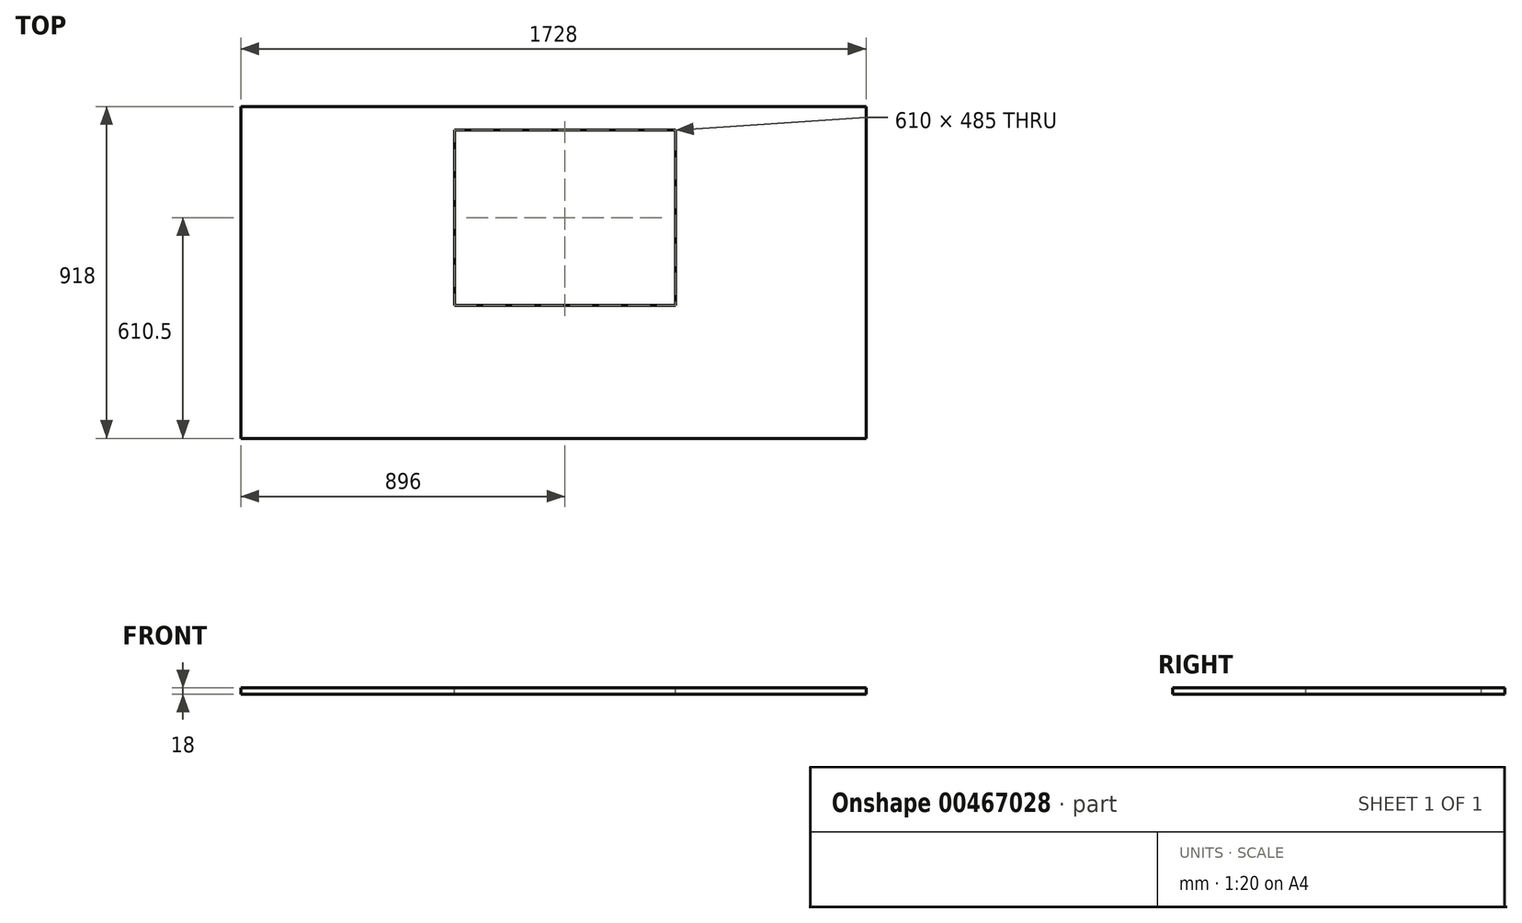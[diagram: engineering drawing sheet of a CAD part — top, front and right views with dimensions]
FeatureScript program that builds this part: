
annotation { "Feature Type Name" : "Feature", "Feature Type Description" : "" }
export const myFeature = defineFeature(function(context is Context, id is Id, definition is map)
    precondition{}
    {
        {
            var Q0;
            Q0=qCreatedBy(makeId("Top.planeOp"),FACE);
            var sketch = newSketch(context, id + "F0", { "sketchPlane" : qUnion([Q0])});
            skLineSegment(sketch, "E0.bottom", {"start": v(0, 918) * mm, "end": v(1728, 918) * mm});
            skLineSegment(sketch, "E0.top", {"start": v(0, 0) * mm, "end": v(1728, 0) * mm});
            skLineSegment(sketch, "E0.left", {"start": v(0, 918) * mm, "end": v(0, 0) * mm});
            skLineSegment(sketch, "E0.right", {"start": v(1728, 918) * mm, "end": v(1728, 0) * mm});
            skSolve(sketch);
        }
        {
            var Q0;
            Q0 = qSketchRegion(id + "F0", true);
            extrude(context, id + "F1", {"entities" : qUnion([Q0]), "depth" : 18 * mm});
        }
        {
            var Q0;
            Q0=makeQuery(id+"F1.opExtrude","CAP_FACE",FACE,{"disambiguationData":[OSD([sQuery(id+"F0.wireOp",EDGE,"E0.bottom"),sQuery(id+"F0.wireOp",EDGE,"E0.top"),sQuery(id+"F0.wireOp",EDGE,"E0.left"),sQuery(id+"F0.wireOp",EDGE,"E0.right")])],"isStart":false});
            var sketch = newSketch(context, id + "F2", { "sketchPlane" : qUnion([Q0])});
            skLineSegment(sketch, "E1.bottom", {"start": v(591, 853) * mm, "end": v(1201, 853) * mm});
            skLineSegment(sketch, "E1.top", {"start": v(591, 368) * mm, "end": v(1201, 368) * mm});
            skLineSegment(sketch, "E1.left", {"start": v(591, 853) * mm, "end": v(591, 368) * mm});
            skLineSegment(sketch, "E1.right", {"start": v(1201, 853) * mm, "end": v(1201, 368) * mm});
            skSolve(sketch);
        }
        {
            var Q0;
            Q0 = qSketchRegion(id + "F2", true);
            extrude(context, id + "F3", {"entities" : qUnion([Q0]), "operationType" : NewBodyOperationType.REMOVE, "endBound" : BoundingType.THROUGH_ALL, "oppositeDirection" : true, "depth" : 25 * mm, "offsetDistance" : 25 * mm});
        }
    });
